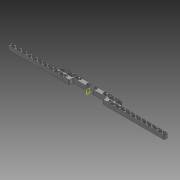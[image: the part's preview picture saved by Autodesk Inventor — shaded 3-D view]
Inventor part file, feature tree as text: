
AUTODESK INVENTOR PART (.ipt)
format: ipt  version: 2011 SP2 (Build 150309200, 309)  size: 1,116,672 bytes
history: native  units: mm
features: fillet x13, extrude x8, projected_geometry x8, sketch x6, plane x1, mirror x1
ambient origin geometry x8: Origin, YZ Plane, XZ Plane, XY Plane, X Axis, Y Axis, Z Axis, Center Point
feature tree (37):
  sketch  "Sketch1"  dims[d14=1.0mm d16=1.0mm]
  extrude  "Extrusion11"  Depth=1.0mm
  extrude  "Extrusion12"  Depth=1.0mm
  extrude  "Extrusion13"  Depth=16.580628mm
  extrude  "Extrusion14"  Depth=0.5mm
  extrude  "Extrusion15"  Depth=0.5mm
  extrude  "Extrusion16"  Depth=0.5mm
  fillet  "Fillet13"  Radius=0.5mm
  fillet  "Fillet14"  Radius=0.5mm
  fillet  "Fillet15"  Radius=0.5mm
  fillet  "Fillet16"  Radius=0.5mm
  fillet  "Fillet17"  Radius=0.5mm
  fillet  "Fillet18"  Radius=0.5mm
  fillet  "Fillet19"  Radius=0.5mm
  fillet  "Fillet20"  Radius=0.5mm
  fillet  "Fillet21"  Radius=0.5mm
  fillet  "Fillet22"  Radius=0.5mm
  fillet  "Fillet25"  Radius=0.5mm
  extrude  "Extrusion17"  Depth=0.5mm
  fillet  "Fillet26"  Radius=0.5mm
  extrude  "Extrusion18"  Depth=0.5mm
  fillet  "Fillet27"  Radius=0.5mm
  plane  "Work Plane2"
  mirror  "Mirror2"
  sketch  "Sketch11"  dims[d23=1.0mm d24=1.0mm]
  projected_geometry  "Projected Loop7"
  sketch  "Sketch12"  dims[d25=1.0mm d30=16.580628mm]
  projected_geometry  "Projected Loop8"
  projected_geometry  "Projected Loop9"
  sketch  "Sketch13"  dims[d32=1.0mm d62=0.5mm]
  sketch  "Sketch14"  dims[d64=0.5mm d65=0.5mm]
  sketch  "Sketch15"  dims[d66=0.5mm d68=0.5mm d69=0.5mm d70=0.5mm d71=0.5mm d72=0.5mm d73=0.5mm d74=0.5mm d75=0.5mm d76=0.5mm d77=0.5mm d78=0.5mm d79=0.5mm d80=0.5mm d81=0.5mm d82=0.5mm d83=0.5mm d84=0.5mm d85=0.5mm d86=0.5mm d87=0.5mm d88=0.5mm d89=0.5mm d90=0.5mm d91=0.5mm d92=0.5mm d93=0.5mm d94=0.5mm d95=0.5mm d96=0.5mm d97=0.5mm d98=0.5mm d99=0.5mm d100=0.5mm d101=0.5mm d102=0.5mm d103=0.5mm d104=0.5mm d106=0.5mm d107=0.5mm d108=0.5mm d109=0.5mm d115=14.209mm d116=3.912mm d120=5.45mm d121=3.75mm d122=1.875mm d124=2.725mm d126=3.060539mm d166=1.0mm d167=0.5mm d169=0.5mm d171=0.5mm d172=0.5mm d173=0.5mm d174=0.5mm d175=0.5mm d176=0.5mm d177=0.5mm d178=0.5mm d179=0.5mm d180=0.5mm d181=0.5mm d182=0.5mm d183=13.0mm d184=5.0mm d185=10.0mm d186=3.45mm d187=1.956mm d188=28.816511mm d189=34.516421mm d190=9.0mm d191=1.0mm d192=172.0mm d193=35.152794mm d194=10.0mm d195=0.0mm d196=10.0mm d197=0.0mm d198=6.85mm d199=0.0mm d200=10.0mm d201=8.0mm d202=0.0mm d203=14.835299mm d204=10.0mm d205=0.0mm d206=16.580628mm d207=10.0mm d208=0.0mm d209=1.0mm d210=1.0mm d211=0.5mm d212=1.75mm d213=0.2mm d214=1.0mm d215=0.5mm d216=0.5mm d217=0.5mm d218=1.0mm d221=2.25mm d222=10.0mm d223=0.0mm d224=0.75mm d225=10.0mm d226=0.0mm d227=0.5mm d228=-175.0mm]
  projected_geometry  "Projected Loop10"
  projected_geometry  "Projected Loop11"
  projected_geometry  "Projected Loop12"
  projected_geometry  "Projected Loop13"
  projected_geometry  "Projected Loop14"
